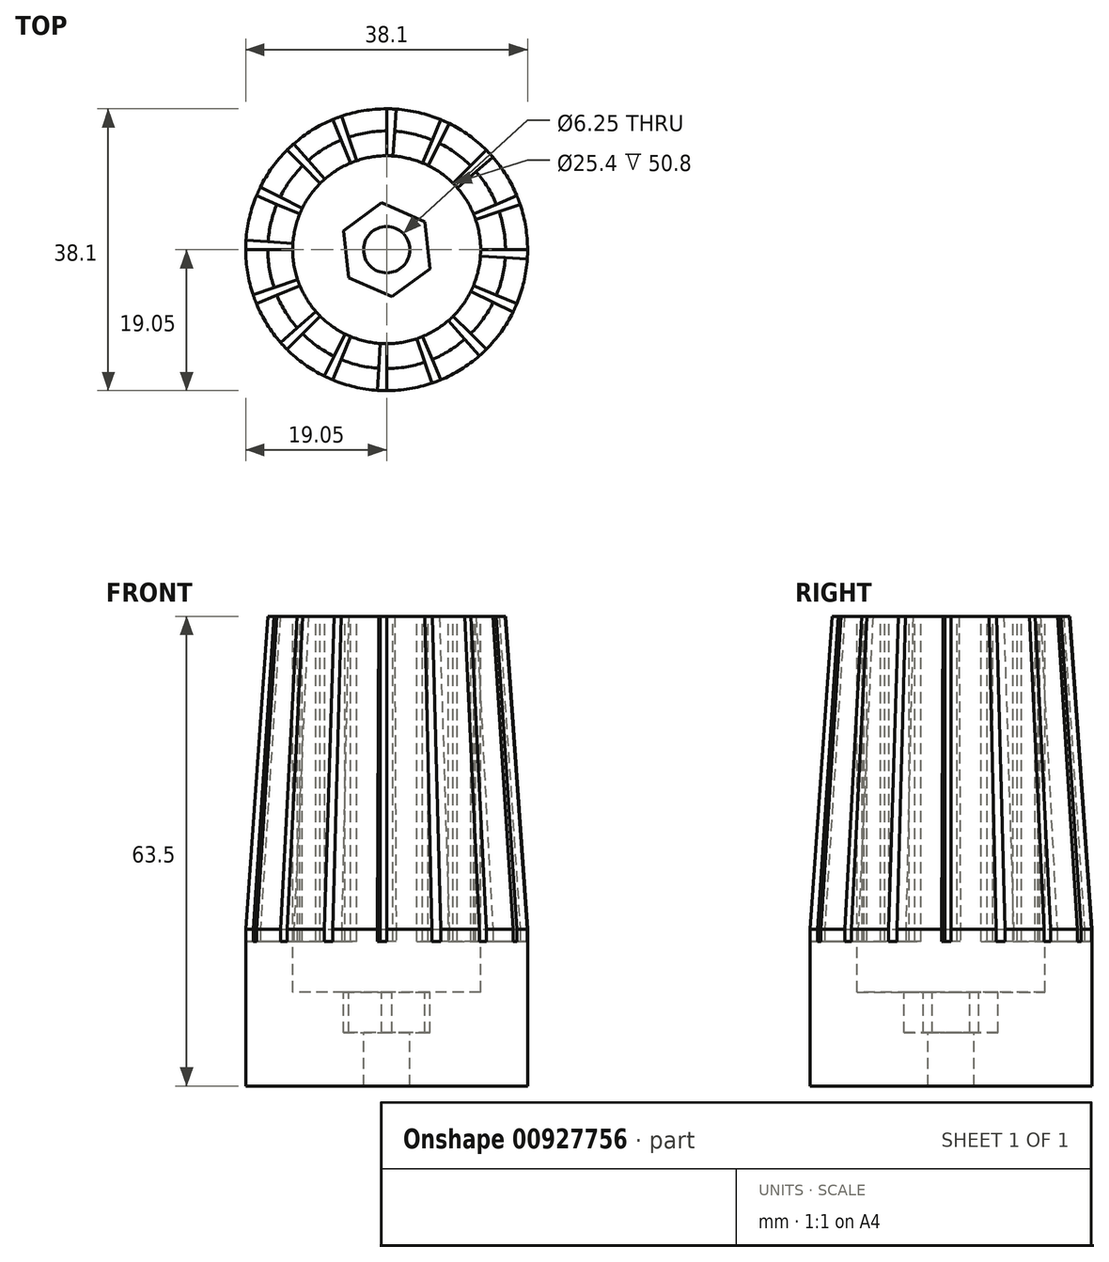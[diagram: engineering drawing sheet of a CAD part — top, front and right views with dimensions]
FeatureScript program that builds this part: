
annotation { "Feature Type Name" : "Feature", "Feature Type Description" : "" }
export const myFeature = defineFeature(function(context is Context, id is Id, definition is map)
    precondition{}
    {
        {
            var Q0;
            Q0=qCreatedBy(makeId("Top.planeOp"),FACE);
            var sketch = newSketch(context, id + "F0", { "sketchPlane" : qUnion([Q0])});
            skCircle(sketch, "E0", {"center": v(0, 0) * mm, "radius": 19.05 * mm});
            skSolve(sketch);
        }
        {
            var Q0;
            Q0=qSketchRegion(id+"F0",true);
            extrude(context, id + "F1", {"entities" : qUnion([Q0]), "depth" : 63.5 * mm, "offsetDistance" : 25.4 * mm});
        }
        {
            var Q0;
            Q0=qCreatedBy(makeId("Right.planeOp"),FACE);
            var sketch = newSketch(context, id + "F2", { "sketchPlane" : qUnion([Q0])});
            skLineSegment(sketch, "E1", {"start": v(0, 0) * mm, "end": v(-26.99, 0) * mm});
            skLineSegment(sketch, "E2", {"start": v(-26.99, 0) * mm, "end": v(-26.43, 6.35) * mm});
            skLineSegment(sketch, "E3", {"start": v(-26.43, 6.35) * mm, "end": v(-43.98, 6.35) * mm});
            skLineSegment(sketch, "E4", {"start": v(-43.98, 6.35) * mm, "end": v(-43.98, 0) * mm});
            skLineSegment(sketch, "E5", {"start": v(-43.98, 0) * mm, "end": v(-26.99, 0) * mm});
            skLineSegment(sketch, "E6", {"start": v(0, 0) * mm, "end": v(0, -23.56) * mm});
            skSolve(sketch);
        }
        {
            var Q0;
            Q0=makeQuery(id+"F1.opExtrude","CAP_FACE",FACE,{"disambiguationData":[OSD([sQuery(id+"F0.wireOp",EDGE,"E0")])],"isStart":false});
            var sketch = newSketch(context, id + "F3", { "sketchPlane" : qUnion([Q0])});
            skCircle(sketch, "E7", {"center": v(0, 0) * mm, "radius": 12.7 * mm});
            skSolve(sketch);
        }
        {
            var Q0;
            Q0=makeQuery(id+"F3.imprint","IMPRINT",FACE,{"disambiguationData":[TD([[makeQuery(id+"F3.imprint","IMPRINT",EDGE,{"derivedFrom":sQuery(id+"F3.wireOp",EDGE,"E7")}),1.0]])]});
            extrude(context, id + "F4", {"entities" : qUnion([Q0]), "operationType" : NewBodyOperationType.REMOVE, "oppositeDirection" : true, "depth" : 50.8 * mm, "offsetDistance" : 25.4 * mm});
        }
        {
            var Q0;
            Q0=makeQuery(id+"F1.opExtrude","CAP_FACE",FACE,{"disambiguationData":[OSD([sQuery(id+"F0.wireOp",EDGE,"E0")])],"isStart":false});
            var sketch = newSketch(context, id + "F5", { "sketchPlane" : qUnion([Q0])});
            skLineSegment(sketch, "E8", {"start": v(0, 0) * mm, "end": v(0, 38.1) * mm});
            skLineSegment(sketch, "E9", {"start": v(0, 38.1) * mm, "end": v(2.54, 38.1) * mm});
            skLineSegment(sketch, "E10", {"start": v(2.54, 38.1) * mm, "end": v(0, 0) * mm});
            skLineSegment(sketch, "E11.1.0", {"start": v(0, 0) * mm, "end": v(-14.58, 35.2) * mm});
            skLineSegment(sketch, "E11.1.1", {"start": v(-12.23, 36.17) * mm, "end": v(0, 0) * mm});
            skLineSegment(sketch, "E11.1.2", {"start": v(-14.58, 35.2) * mm, "end": v(-12.23, 36.17) * mm});
            skLineSegment(sketch, "E11.2.0", {"start": v(0, 0) * mm, "end": v(-26.94, 26.94) * mm});
            skLineSegment(sketch, "E11.2.1", {"start": v(-25.14, 28.74) * mm, "end": v(0, 0) * mm});
            skLineSegment(sketch, "E11.2.2", {"start": v(-26.94, 26.94) * mm, "end": v(-25.14, 28.74) * mm});
            skLineSegment(sketch, "E11.3.0", {"start": v(0, 0) * mm, "end": v(-35.2, 14.58) * mm});
            skLineSegment(sketch, "E11.3.1", {"start": v(-34.23, 16.93) * mm, "end": v(0, 0) * mm});
            skLineSegment(sketch, "E11.3.2", {"start": v(-35.2, 14.58) * mm, "end": v(-34.23, 16.93) * mm});
            skLineSegment(sketch, "E11.4.0", {"start": v(0, 0) * mm, "end": v(-38.1, 0) * mm});
            skLineSegment(sketch, "E11.4.1", {"start": v(-38.1, 2.54) * mm, "end": v(0, 0) * mm});
            skLineSegment(sketch, "E11.4.2", {"start": v(-38.1, 0) * mm, "end": v(-38.1, 2.54) * mm});
            skLineSegment(sketch, "E11.5.0", {"start": v(0, 0) * mm, "end": v(-35.2, -14.58) * mm});
            skLineSegment(sketch, "E11.5.1", {"start": v(-36.17, -12.23) * mm, "end": v(0, 0) * mm});
            skLineSegment(sketch, "E11.5.2", {"start": v(-35.2, -14.58) * mm, "end": v(-36.17, -12.23) * mm});
            skLineSegment(sketch, "E11.6.0", {"start": v(0, 0) * mm, "end": v(-26.94, -26.94) * mm});
            skLineSegment(sketch, "E11.6.1", {"start": v(-28.74, -25.14) * mm, "end": v(0, 0) * mm});
            skLineSegment(sketch, "E11.6.2", {"start": v(-26.94, -26.94) * mm, "end": v(-28.74, -25.14) * mm});
            skLineSegment(sketch, "E11.7.0", {"start": v(0, 0) * mm, "end": v(-14.58, -35.2) * mm});
            skLineSegment(sketch, "E11.7.1", {"start": v(-16.93, -34.23) * mm, "end": v(0, 0) * mm});
            skLineSegment(sketch, "E11.7.2", {"start": v(-14.58, -35.2) * mm, "end": v(-16.93, -34.23) * mm});
            skLineSegment(sketch, "E11.8.0", {"start": v(0, 0) * mm, "end": v(0, -38.1) * mm});
            skLineSegment(sketch, "E11.8.1", {"start": v(-2.54, -38.1) * mm, "end": v(0, 0) * mm});
            skLineSegment(sketch, "E11.8.2", {"start": v(0, -38.1) * mm, "end": v(-2.54, -38.1) * mm});
            skLineSegment(sketch, "E11.9.0", {"start": v(0, 0) * mm, "end": v(14.58, -35.2) * mm});
            skLineSegment(sketch, "E11.9.1", {"start": v(12.23, -36.17) * mm, "end": v(0, 0) * mm});
            skLineSegment(sketch, "E11.9.2", {"start": v(14.58, -35.2) * mm, "end": v(12.23, -36.17) * mm});
            skLineSegment(sketch, "E11.10.0", {"start": v(0, 0) * mm, "end": v(26.94, -26.94) * mm});
            skLineSegment(sketch, "E11.10.1", {"start": v(25.14, -28.74) * mm, "end": v(0, 0) * mm});
            skLineSegment(sketch, "E11.10.2", {"start": v(26.94, -26.94) * mm, "end": v(25.14, -28.74) * mm});
            skLineSegment(sketch, "E11.11.0", {"start": v(0, 0) * mm, "end": v(35.2, -14.58) * mm});
            skLineSegment(sketch, "E11.11.1", {"start": v(34.23, -16.93) * mm, "end": v(0, 0) * mm});
            skLineSegment(sketch, "E11.11.2", {"start": v(35.2, -14.58) * mm, "end": v(34.23, -16.93) * mm});
            skLineSegment(sketch, "E11.12.0", {"start": v(0, 0) * mm, "end": v(38.1, 0) * mm});
            skLineSegment(sketch, "E11.12.1", {"start": v(38.1, -2.54) * mm, "end": v(0, 0) * mm});
            skLineSegment(sketch, "E11.12.2", {"start": v(38.1, 0) * mm, "end": v(38.1, -2.54) * mm});
            skLineSegment(sketch, "E11.13.0", {"start": v(0, 0) * mm, "end": v(35.2, 14.58) * mm});
            skLineSegment(sketch, "E11.13.1", {"start": v(36.17, 12.23) * mm, "end": v(0, 0) * mm});
            skLineSegment(sketch, "E11.13.2", {"start": v(35.2, 14.58) * mm, "end": v(36.17, 12.23) * mm});
            skLineSegment(sketch, "E11.14.0", {"start": v(0, 0) * mm, "end": v(26.94, 26.94) * mm});
            skLineSegment(sketch, "E11.14.1", {"start": v(28.74, 25.14) * mm, "end": v(0, 0) * mm});
            skLineSegment(sketch, "E11.14.2", {"start": v(26.94, 26.94) * mm, "end": v(28.74, 25.14) * mm});
            skLineSegment(sketch, "E11.15.0", {"start": v(0, 0) * mm, "end": v(14.58, 35.2) * mm});
            skLineSegment(sketch, "E11.15.1", {"start": v(16.93, 34.23) * mm, "end": v(0, 0) * mm});
            skLineSegment(sketch, "E11.15.2", {"start": v(14.58, 35.2) * mm, "end": v(16.93, 34.23) * mm});
            skPoint(sketch, "E11.center", {"position": v(0, 0) * mm});
            skSolve(sketch);
        }
        {
            var Q0;
            Q0=qSketchRegion(id+"F5",true);
            var Q1;
            Q1=makeQuery(id+"F4.boolean.opBoolean","COPY",FACE,{"derivedFrom":makeQuery(id+"F4.opExtrude","CAP_FACE",FACE,{"disambiguationData":[OSD([sQuery(id+"F3.wireOp",EDGE,"E7")])],"isStart":false})});
            extrude(context, id + "F6", {"entities" : qUnion([Q0]), "operationType" : NewBodyOperationType.REMOVE, "oppositeDirection" : true, "depth" : 43.94 * mm, "endBoundEntityFace" : qUnion([Q1]), "offsetDistance" : 25.4 * mm});
        }
        {
            var Q0;
            Q0=makeQuery(id+"F6.boolean.opBoolean","MERGE",FACE,{"derivedFrom":[makeQuery(id+"F4.boolean.opBoolean","COPY",FACE,{"derivedFrom":makeQuery(id+"F4.opExtrude","CAP_FACE",FACE,{"disambiguationData":[OSD([sQuery(id+"F3.wireOp",EDGE,"E7")])],"isStart":false})})],"fromTools":[makeQuery(id+"F6.opExtrude","CAP_FACE",FACE,{"disambiguationData":[OSD([sQuery(id+"F5.wireOp",EDGE,"E8"),sQuery(id+"F5.wireOp",EDGE,"E9"),sQuery(id+"F5.wireOp",EDGE,"E10")])],"isStart":false}),makeQuery(id+"F6.opExtrude","CAP_FACE",FACE,{"disambiguationData":[OSD([sQuery(id+"F5.wireOp",EDGE,"E11.1.0"),sQuery(id+"F5.wireOp",EDGE,"E11.1.1"),sQuery(id+"F5.wireOp",EDGE,"E11.1.2")])],"isStart":false}),makeQuery(id+"F6.opExtrude","CAP_FACE",FACE,{"disambiguationData":[OSD([sQuery(id+"F5.wireOp",EDGE,"E11.2.0"),sQuery(id+"F5.wireOp",EDGE,"E11.2.1"),sQuery(id+"F5.wireOp",EDGE,"E11.2.2")])],"isStart":false}),makeQuery(id+"F6.opExtrude","CAP_FACE",FACE,{"disambiguationData":[OSD([sQuery(id+"F5.wireOp",EDGE,"E11.3.0"),sQuery(id+"F5.wireOp",EDGE,"E11.3.1"),sQuery(id+"F5.wireOp",EDGE,"E11.3.2")])],"isStart":false}),makeQuery(id+"F6.opExtrude","CAP_FACE",FACE,{"disambiguationData":[OSD([sQuery(id+"F5.wireOp",EDGE,"E11.4.0"),sQuery(id+"F5.wireOp",EDGE,"E11.4.1"),sQuery(id+"F5.wireOp",EDGE,"E11.4.2")])],"isStart":false}),makeQuery(id+"F6.opExtrude","CAP_FACE",FACE,{"disambiguationData":[OSD([sQuery(id+"F5.wireOp",EDGE,"E11.5.0"),sQuery(id+"F5.wireOp",EDGE,"E11.5.1"),sQuery(id+"F5.wireOp",EDGE,"E11.5.2")])],"isStart":false}),makeQuery(id+"F6.opExtrude","CAP_FACE",FACE,{"disambiguationData":[OSD([sQuery(id+"F5.wireOp",EDGE,"E11.6.0"),sQuery(id+"F5.wireOp",EDGE,"E11.6.1"),sQuery(id+"F5.wireOp",EDGE,"E11.6.2")])],"isStart":false}),makeQuery(id+"F6.opExtrude","CAP_FACE",FACE,{"disambiguationData":[OSD([sQuery(id+"F5.wireOp",EDGE,"E11.7.0"),sQuery(id+"F5.wireOp",EDGE,"E11.7.1"),sQuery(id+"F5.wireOp",EDGE,"E11.7.2")])],"isStart":false}),makeQuery(id+"F6.opExtrude","CAP_FACE",FACE,{"disambiguationData":[OSD([sQuery(id+"F5.wireOp",EDGE,"E11.8.0"),sQuery(id+"F5.wireOp",EDGE,"E11.8.1"),sQuery(id+"F5.wireOp",EDGE,"E11.8.2")])],"isStart":false}),makeQuery(id+"F6.opExtrude","CAP_FACE",FACE,{"disambiguationData":[OSD([sQuery(id+"F5.wireOp",EDGE,"E11.9.0"),sQuery(id+"F5.wireOp",EDGE,"E11.9.1"),sQuery(id+"F5.wireOp",EDGE,"E11.9.2")])],"isStart":false}),makeQuery(id+"F6.opExtrude","CAP_FACE",FACE,{"disambiguationData":[OSD([sQuery(id+"F5.wireOp",EDGE,"E11.10.0"),sQuery(id+"F5.wireOp",EDGE,"E11.10.1"),sQuery(id+"F5.wireOp",EDGE,"E11.10.2")])],"isStart":false}),makeQuery(id+"F6.opExtrude","CAP_FACE",FACE,{"disambiguationData":[OSD([sQuery(id+"F5.wireOp",EDGE,"E11.11.0"),sQuery(id+"F5.wireOp",EDGE,"E11.11.1"),sQuery(id+"F5.wireOp",EDGE,"E11.11.2")])],"isStart":false}),makeQuery(id+"F6.opExtrude","CAP_FACE",FACE,{"disambiguationData":[OSD([sQuery(id+"F5.wireOp",EDGE,"E11.12.0"),sQuery(id+"F5.wireOp",EDGE,"E11.12.1"),sQuery(id+"F5.wireOp",EDGE,"E11.12.2")])],"isStart":false}),makeQuery(id+"F6.opExtrude","CAP_FACE",FACE,{"disambiguationData":[OSD([sQuery(id+"F5.wireOp",EDGE,"E11.13.0"),sQuery(id+"F5.wireOp",EDGE,"E11.13.1"),sQuery(id+"F5.wireOp",EDGE,"E11.13.2")])],"isStart":false}),makeQuery(id+"F6.opExtrude","CAP_FACE",FACE,{"disambiguationData":[OSD([sQuery(id+"F5.wireOp",EDGE,"E11.14.0"),sQuery(id+"F5.wireOp",EDGE,"E11.14.1"),sQuery(id+"F5.wireOp",EDGE,"E11.14.2")])],"isStart":false}),makeQuery(id+"F6.opExtrude","CAP_FACE",FACE,{"disambiguationData":[OSD([sQuery(id+"F5.wireOp",EDGE,"E11.15.0"),sQuery(id+"F5.wireOp",EDGE,"E11.15.1"),sQuery(id+"F5.wireOp",EDGE,"E11.15.2")])],"isStart":false})]});
            var sketch = newSketch(context, id + "F7", { "sketchPlane" : qUnion([Q0])});
            skCircle(sketch, "E12", {"center": v(0, 0) * mm, "radius": 3.13 * mm});
            skSolve(sketch);
        }
        {
            var Q0;
            Q0 = qSketchRegion(id + "F7", true);
            extrude(context, id + "F8", {"entities" : qUnion([Q0]), "operationType" : NewBodyOperationType.REMOVE, "oppositeDirection" : true, "depth" : 53.6 * mm, "offsetDistance" : 25.4 * mm});
        }
        {
            var Q0;
            Q0=makeQuery(id+"F6.boolean.opBoolean","MERGE",FACE,{"derivedFrom":[makeQuery(id+"F4.boolean.opBoolean","COPY",FACE,{"derivedFrom":makeQuery(id+"F4.opExtrude","CAP_FACE",FACE,{"disambiguationData":[OSD([sQuery(id+"F3.wireOp",EDGE,"E7")])],"isStart":false})})],"fromTools":[makeQuery(id+"F6.opExtrude","CAP_FACE",FACE,{"disambiguationData":[OSD([sQuery(id+"F5.wireOp",EDGE,"E8"),sQuery(id+"F5.wireOp",EDGE,"E9"),sQuery(id+"F5.wireOp",EDGE,"E10")])],"isStart":false}),makeQuery(id+"F6.opExtrude","CAP_FACE",FACE,{"disambiguationData":[OSD([sQuery(id+"F5.wireOp",EDGE,"E11.1.0"),sQuery(id+"F5.wireOp",EDGE,"E11.1.1"),sQuery(id+"F5.wireOp",EDGE,"E11.1.2")])],"isStart":false}),makeQuery(id+"F6.opExtrude","CAP_FACE",FACE,{"disambiguationData":[OSD([sQuery(id+"F5.wireOp",EDGE,"E11.2.0"),sQuery(id+"F5.wireOp",EDGE,"E11.2.1"),sQuery(id+"F5.wireOp",EDGE,"E11.2.2")])],"isStart":false}),makeQuery(id+"F6.opExtrude","CAP_FACE",FACE,{"disambiguationData":[OSD([sQuery(id+"F5.wireOp",EDGE,"E11.3.0"),sQuery(id+"F5.wireOp",EDGE,"E11.3.1"),sQuery(id+"F5.wireOp",EDGE,"E11.3.2")])],"isStart":false}),makeQuery(id+"F6.opExtrude","CAP_FACE",FACE,{"disambiguationData":[OSD([sQuery(id+"F5.wireOp",EDGE,"E11.4.0"),sQuery(id+"F5.wireOp",EDGE,"E11.4.1"),sQuery(id+"F5.wireOp",EDGE,"E11.4.2")])],"isStart":false}),makeQuery(id+"F6.opExtrude","CAP_FACE",FACE,{"disambiguationData":[OSD([sQuery(id+"F5.wireOp",EDGE,"E11.5.0"),sQuery(id+"F5.wireOp",EDGE,"E11.5.1"),sQuery(id+"F5.wireOp",EDGE,"E11.5.2")])],"isStart":false}),makeQuery(id+"F6.opExtrude","CAP_FACE",FACE,{"disambiguationData":[OSD([sQuery(id+"F5.wireOp",EDGE,"E11.6.0"),sQuery(id+"F5.wireOp",EDGE,"E11.6.1"),sQuery(id+"F5.wireOp",EDGE,"E11.6.2")])],"isStart":false}),makeQuery(id+"F6.opExtrude","CAP_FACE",FACE,{"disambiguationData":[OSD([sQuery(id+"F5.wireOp",EDGE,"E11.7.0"),sQuery(id+"F5.wireOp",EDGE,"E11.7.1"),sQuery(id+"F5.wireOp",EDGE,"E11.7.2")])],"isStart":false}),makeQuery(id+"F6.opExtrude","CAP_FACE",FACE,{"disambiguationData":[OSD([sQuery(id+"F5.wireOp",EDGE,"E11.8.0"),sQuery(id+"F5.wireOp",EDGE,"E11.8.1"),sQuery(id+"F5.wireOp",EDGE,"E11.8.2")])],"isStart":false}),makeQuery(id+"F6.opExtrude","CAP_FACE",FACE,{"disambiguationData":[OSD([sQuery(id+"F5.wireOp",EDGE,"E11.9.0"),sQuery(id+"F5.wireOp",EDGE,"E11.9.1"),sQuery(id+"F5.wireOp",EDGE,"E11.9.2")])],"isStart":false}),makeQuery(id+"F6.opExtrude","CAP_FACE",FACE,{"disambiguationData":[OSD([sQuery(id+"F5.wireOp",EDGE,"E11.10.0"),sQuery(id+"F5.wireOp",EDGE,"E11.10.1"),sQuery(id+"F5.wireOp",EDGE,"E11.10.2")])],"isStart":false}),makeQuery(id+"F6.opExtrude","CAP_FACE",FACE,{"disambiguationData":[OSD([sQuery(id+"F5.wireOp",EDGE,"E11.11.0"),sQuery(id+"F5.wireOp",EDGE,"E11.11.1"),sQuery(id+"F5.wireOp",EDGE,"E11.11.2")])],"isStart":false}),makeQuery(id+"F6.opExtrude","CAP_FACE",FACE,{"disambiguationData":[OSD([sQuery(id+"F5.wireOp",EDGE,"E11.12.0"),sQuery(id+"F5.wireOp",EDGE,"E11.12.1"),sQuery(id+"F5.wireOp",EDGE,"E11.12.2")])],"isStart":false}),makeQuery(id+"F6.opExtrude","CAP_FACE",FACE,{"disambiguationData":[OSD([sQuery(id+"F5.wireOp",EDGE,"E11.13.0"),sQuery(id+"F5.wireOp",EDGE,"E11.13.1"),sQuery(id+"F5.wireOp",EDGE,"E11.13.2")])],"isStart":false}),makeQuery(id+"F6.opExtrude","CAP_FACE",FACE,{"disambiguationData":[OSD([sQuery(id+"F5.wireOp",EDGE,"E11.14.0"),sQuery(id+"F5.wireOp",EDGE,"E11.14.1"),sQuery(id+"F5.wireOp",EDGE,"E11.14.2")])],"isStart":false}),makeQuery(id+"F6.opExtrude","CAP_FACE",FACE,{"disambiguationData":[OSD([sQuery(id+"F5.wireOp",EDGE,"E11.15.0"),sQuery(id+"F5.wireOp",EDGE,"E11.15.1"),sQuery(id+"F5.wireOp",EDGE,"E11.15.2")])],"isStart":false})]});
            var sketch = newSketch(context, id + "F9", { "sketchPlane" : qUnion([Q0])});
            skCircle(sketch, "E13.cCircle", {"center": v(0, 0) * mm, "radius": 5.53 * mm, "construction": true});
            skLineSegment(sketch, "E13.0", {"start": v(5.84, -2.56) * mm, "end": v(0.7, -6.34) * mm});
            skLineSegment(sketch, "E13.1", {"start": v(0.7, -6.34) * mm, "end": v(-5.14, -3.78) * mm});
            skLineSegment(sketch, "E13.2", {"start": v(-5.14, -3.78) * mm, "end": v(-5.84, 2.56) * mm});
            skLineSegment(sketch, "E13.3", {"start": v(-5.84, 2.56) * mm, "end": v(-0.7, 6.34) * mm});
            skLineSegment(sketch, "E13.4", {"start": v(-0.7, 6.34) * mm, "end": v(5.14, 3.78) * mm});
            skLineSegment(sketch, "E13.5", {"start": v(5.14, 3.78) * mm, "end": v(5.84, -2.56) * mm});
            skPoint(sketch, "E13.0.midPoint", {"position": v(3.27, -4.45) * mm});
            skSolve(sketch);
        }
        {
            var Q0;
            Q0 = qSketchRegion(id + "F9", true);
            extrude(context, id + "F10", {"entities" : qUnion([Q0]), "operationType" : NewBodyOperationType.REMOVE, "oppositeDirection" : true, "depth" : 5.5 * mm, "offsetDistance" : 25.4 * mm});
        }
        {
            var Q0;
            Q0=qCreatedBy(makeId("Right.planeOp"),FACE);
            var sketch = newSketch(context, id + "F11", { "sketchPlane" : qUnion([Q0])});
            skLineSegment(sketch, "E14", {"start": v(-19.13, 63.9) * mm, "end": v(-19.13, 20.14) * mm});
            skLineSegment(sketch, "E15", {"start": v(-19.13, 20.14) * mm, "end": v(-16.03, 63.9) * mm});
            skLineSegment(sketch, "E16", {"start": v(-16.03, 63.9) * mm, "end": v(-19.13, 63.9) * mm});
            skLineSegment(sketch, "E17", {"start": v(-19.13, 20.14) * mm, "end": v(0, 18.79) * mm, "construction": true});
            skSolve(sketch);
        }
        {
            var Q0;
            Q0=makeQuery(id+"F11.imprint","IMPRINT",FACE,{"disambiguationData":[TD([[makeQuery(id+"F11.imprint","IMPRINT",EDGE,{"derivedFrom":sQuery(id+"F11.wireOp",EDGE,"E14")}),1.0]])]});
            var Q1;
            Q1=sQuery(id+"F2.wireOp",EDGE,"E6");
            revolve(context, id + "F12", {"operationType" : NewBodyOperationType.REMOVE, "surfaceOperationType" : NewSurfaceOperationType.NEW, "entities" : qUnion([Q0]), "axis" : qUnion([Q1]), "revolveType" : RevolveType.FULL});
        }
    });
